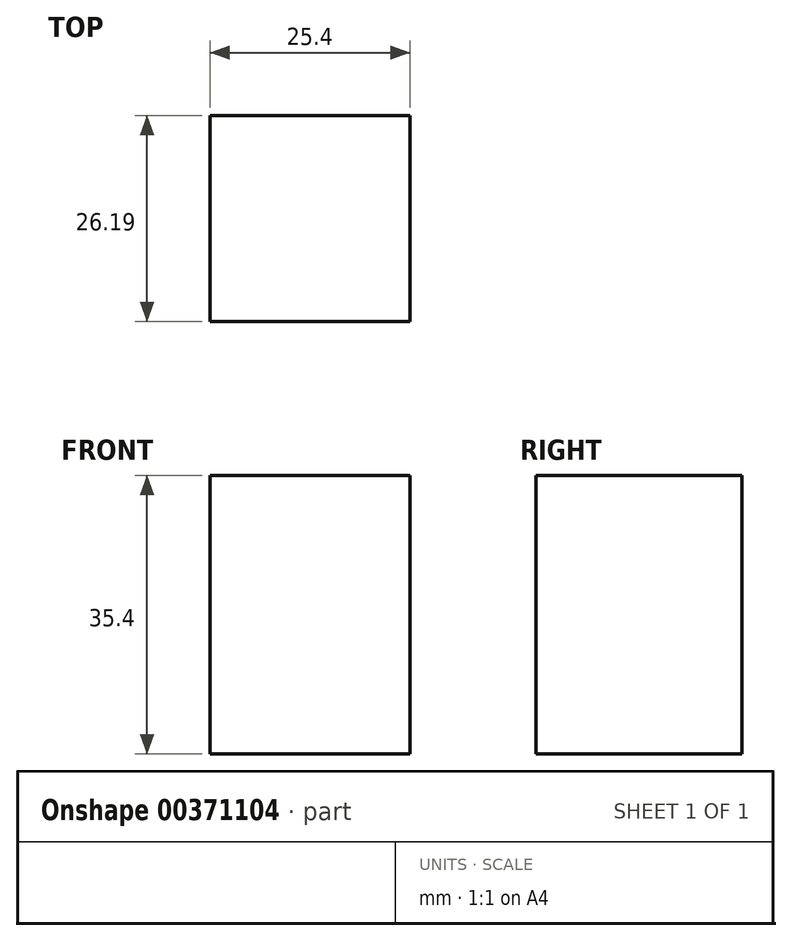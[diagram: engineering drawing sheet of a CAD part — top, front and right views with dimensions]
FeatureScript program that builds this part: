
annotation { "Feature Type Name" : "Feature", "Feature Type Description" : "" }
export const myFeature = defineFeature(function(context is Context, id is Id, definition is map)
    precondition{}
    {
        {
            var Q0;
            Q0=qCreatedBy(makeId("Right.planeOp"),FACE);
            var sketch = newSketch(context, id + "F0", { "sketchPlane" : qUnion([Q0])});
            skLineSegment(sketch, "E0.bottom", {"start": v(26.2, 35.4) * mm, "end": v(0, 35.4) * mm});
            skLineSegment(sketch, "E0.top", {"start": v(26.2, 0) * mm, "end": v(0, 0) * mm});
            skLineSegment(sketch, "E0.left", {"start": v(26.2, 35.4) * mm, "end": v(26.2, 0) * mm});
            skLineSegment(sketch, "E0.right", {"start": v(0, 35.4) * mm, "end": v(0, 0) * mm});
            skSolve(sketch);
        }
        {
            var Q0;
            Q0=makeQuery(id+"F0.imprint","IMPRINT",FACE,{"disambiguationData":[TD([[makeQuery(id+"F0.imprint","IMPRINT",EDGE,{"derivedFrom":sQuery(id+"F0.wireOp",EDGE,"E0.bottom")}),1.0]])]});
            extrude(context, id + "F1", {"entities" : qUnion([Q0]), "depth" : 25.4 * mm});
        }
    });
